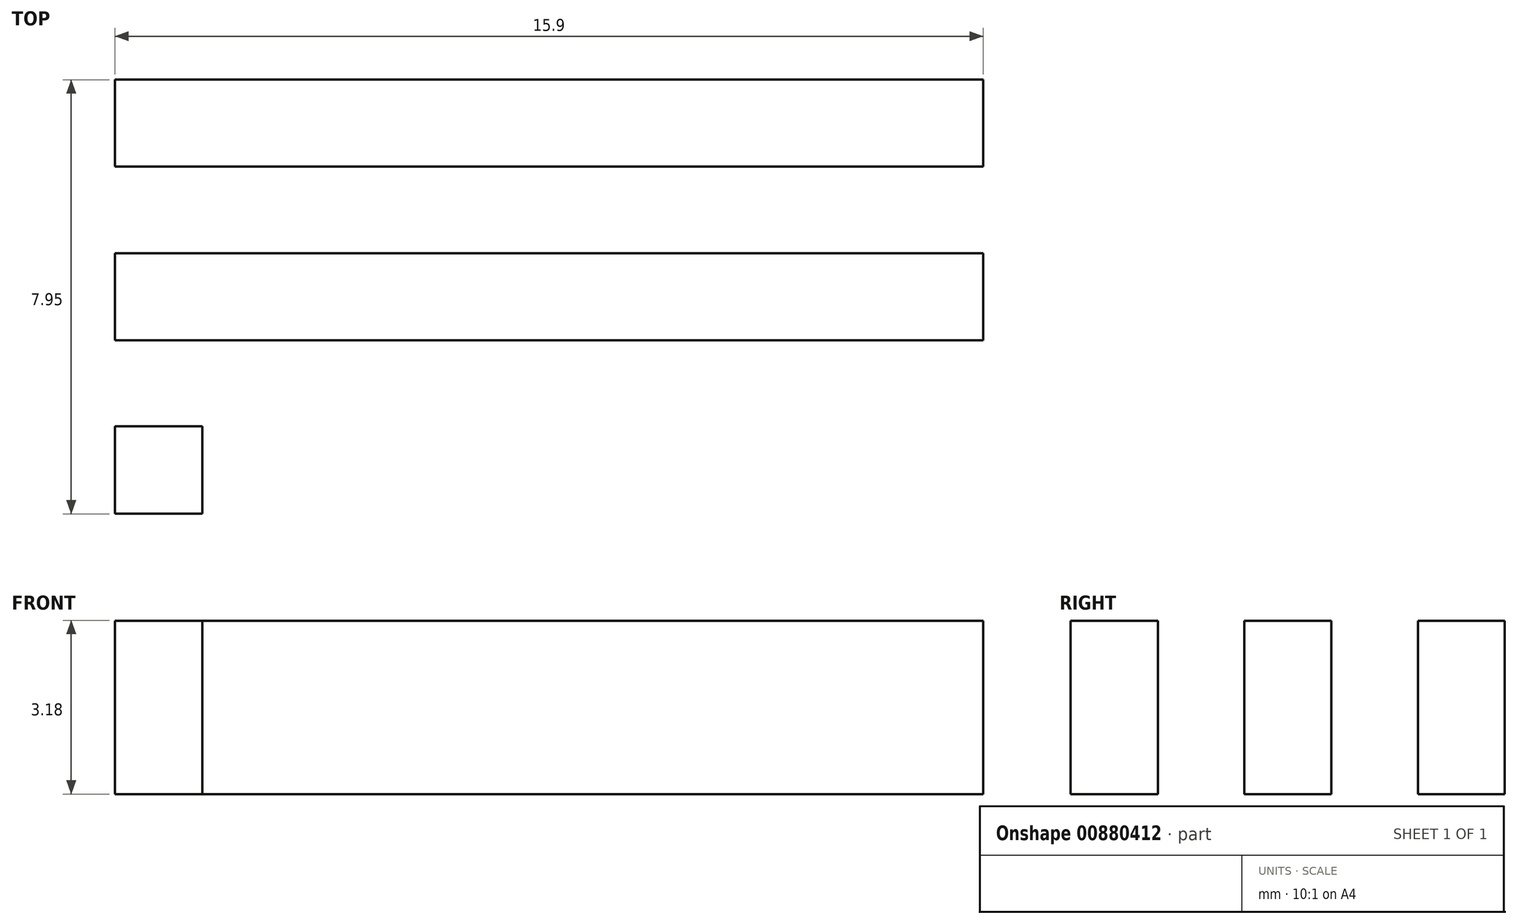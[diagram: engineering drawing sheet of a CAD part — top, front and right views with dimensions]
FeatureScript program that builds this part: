
annotation { "Feature Type Name" : "Feature", "Feature Type Description" : "" }
export const myFeature = defineFeature(function(context is Context, id is Id, definition is map)
    precondition{}
    {
        {
            var Q0;
            Q0=qCreatedBy(makeId("Top.planeOp"),FACE);
            var sketch = newSketch(context, id + "F0", { "sketchPlane" : qUnion([Q0])});
            skLineSegment(sketch, "E0.bottom", {"start": v(-6.6, -3.65) * mm, "end": v(9.3, -3.65) * mm});
            skLineSegment(sketch, "E0.top", {"start": v(-6.6, -11.6) * mm, "end": v(9.3, -11.6) * mm});
            skLineSegment(sketch, "E0.left", {"start": v(-6.6, -3.65) * mm, "end": v(-6.6, -11.6) * mm});
            skLineSegment(sketch, "E0.right", {"start": v(9.3, -3.65) * mm, "end": v(9.3, -11.6) * mm});
            skLineSegment(sketch, "E1", {"start": v(-6.6, -5.24) * mm, "end": v(9.3, -5.24) * mm});
            skLineSegment(sketch, "E2", {"start": v(-6.6, -6.83) * mm, "end": v(9.3, -6.83) * mm});
            skLineSegment(sketch, "E3", {"start": v(-6.6, -8.42) * mm, "end": v(9.3, -8.42) * mm});
            skLineSegment(sketch, "E4", {"start": v(9.3, -10) * mm, "end": v(-6.6, -10) * mm});
            skLineSegment(sketch, "E5", {"start": v(-5, -11.6) * mm, "end": v(-5, -3.65) * mm});
            skLineSegment(sketch, "E6", {"start": v(7.7, -11.6) * mm, "end": v(7.7, -3.65) * mm});
            skLineSegment(sketch, "E7", {"start": v(-6.6, -5.24) * mm, "end": v(-5, -5.24) * mm});
            skLineSegment(sketch, "E8", {"start": v(-5, -5.24) * mm, "end": v(-5, -6.83) * mm});
            skLineSegment(sketch, "E9", {"start": v(-5, -6.83) * mm, "end": v(-6.6, -6.83) * mm});
            skLineSegment(sketch, "E10", {"start": v(-6.6, -5.24) * mm, "end": v(-6.6, -6.83) * mm});
            skLineSegment(sketch, "E11", {"start": v(-6.6, -8.42) * mm, "end": v(-6.6, -10) * mm});
            skLineSegment(sketch, "E12", {"start": v(-5, -10) * mm, "end": v(-5, -8.42) * mm});
            skLineSegment(sketch, "E13", {"start": v(-5, -8.42) * mm, "end": v(-6.6, -8.42) * mm});
            skLineSegment(sketch, "E14", {"start": v(7.7, -5.24) * mm, "end": v(9.3, -5.24) * mm});
            skLineSegment(sketch, "E15", {"start": v(9.3, -6.83) * mm, "end": v(7.7, -6.83) * mm});
            skLineSegment(sketch, "E16", {"start": v(7.7, -6.83) * mm, "end": v(7.7, -5.24) * mm});
            skLineSegment(sketch, "E17", {"start": v(7.7, -10) * mm, "end": v(9.3, -10) * mm});
            skLineSegment(sketch, "E18", {"start": v(9.3, -11.6) * mm, "end": v(7.7, -11.6) * mm});
            skLineSegment(sketch, "E19", {"start": v(9.3, -10) * mm, "end": v(9.3, -11.6) * mm});
            skLineSegment(sketch, "E20", {"start": v(7.7, -11.6) * mm, "end": v(7.7, -10) * mm});
            skSolve(sketch);
        }
        {
            var Q0;
            {var subQ0=sQuery(id+"F0.wireOp",EDGE,"E17");Q0=makeQuery(id+"F0.imprint","IMPRINT",FACE,{"disambiguationData":[TD([[makeQuery(id+"F0.imprint","IMPRINT",EDGE,{"derivedFrom":subQ0}),1.0]])]});}
            var Q1;
            {var subQ5=sQuery(id+"F0.wireOp",EDGE,"E7");Q1=makeQuery(id+"F0.imprint","IMPRINT",FACE,{"disambiguationData":[TD([[makeQuery(id+"F0.imprint","IMPRINT",EDGE,{"derivedFrom":subQ5}),1.0]])]});}
            var Q2;
            {var subQ5=sQuery(id+"F0.wireOp",EDGE,"E14");Q2=makeQuery(id+"F0.imprint","IMPRINT",FACE,{"disambiguationData":[TD([[makeQuery(id+"F0.imprint","IMPRINT",EDGE,{"derivedFrom":subQ5}),1.0]])]});}
            var Q3;
            {var subQ5=sQuery(id+"F0.wireOp",EDGE,"E1");Q3=makeQuery(id+"F0.imprint","IMPRINT",FACE,{"disambiguationData":[TD([[makeQuery(id+"F0.imprint","IMPRINT",EDGE,{"derivedFrom":subQ5}),1.0]])]});}
            var Q4;
            {var subQ0=sQuery(id+"F0.wireOp",EDGE,"E2");Q4=makeQuery(id+"F0.imprint","IMPRINT",FACE,{"disambiguationData":[TD([[makeQuery(id+"F0.imprint","IMPRINT",EDGE,{"derivedFrom":subQ0}),-1.0]])]});}
            var Q5;
            {var subQ0=sQuery(id+"F0.wireOp",EDGE,"E0.left");var subQ1=sQuery(id+"F0.wireOp",EDGE,"E0.top");var subQ2=makeQuery(id+"F0.imprint","INTERSECT",VERTEX,{"derivedFrom":[subQ1,subQ0]});Q5=makeQuery(id+"F0.imprint","IMPRINT",FACE,{"disambiguationData":[TD([[makeQuery(id+"F0.imprint","IMPRINT",EDGE,{"disambiguationData":[TD([[subQ2,-1.0]])],"derivedFrom":subQ1}),1.0]])]});}
            var Q6;
            Q6=makeQuery(id+"F0.imprint","IMPRINT",FACE,{"disambiguationData":[TD([[makeQuery(id+"F0.imprint","IMPRINT",EDGE,{"derivedFrom":sQuery(id+"F0.wireOp",EDGE,"E7")}),-1.0]])]});
            var Q7;
            {var subQ0=sQuery(id+"F0.wireOp",EDGE,"E9");Q7=makeQuery(id+"F0.imprint","IMPRINT",FACE,{"disambiguationData":[TD([[makeQuery(id+"F0.imprint","IMPRINT",EDGE,{"derivedFrom":subQ0}),1.0]])]});}
            var Q8;
            {var subQ0=sQuery(id+"F0.wireOp",EDGE,"E11");Q8=makeQuery(id+"F0.imprint","IMPRINT",FACE,{"disambiguationData":[TD([[makeQuery(id+"F0.imprint","IMPRINT",EDGE,{"derivedFrom":subQ0}),1.0]])]});}
            var Q9;
            {var subQ0=sQuery(id+"F0.wireOp",EDGE,"E14");Q9=makeQuery(id+"F0.imprint","IMPRINT",FACE,{"disambiguationData":[TD([[makeQuery(id+"F0.imprint","IMPRINT",EDGE,{"derivedFrom":subQ0}),-1.0]])]});}
            var Q10;
            {var subQ3=sQuery(id+"F0.wireOp",EDGE,"E15");Q10=makeQuery(id+"F0.imprint","IMPRINT",FACE,{"disambiguationData":[TD([[makeQuery(id+"F0.imprint","IMPRINT",EDGE,{"derivedFrom":subQ3}),1.0]])]});}
            var Q11;
            Q11=makeQuery(id+"F0.imprint","IMPRINT",FACE,{"disambiguationData":[TD([[makeQuery(id+"F0.imprint","IMPRINT",EDGE,{"derivedFrom":sQuery(id+"F0.wireOp",EDGE,"E17")}),-1.0]])]});
            var Q12;
            Q12=makeQuery(id+"F0.imprint","IMPRINT",FACE,{"disambiguationData":[TD([[makeQuery(id+"F0.imprint","IMPRINT",EDGE,{"derivedFrom":sQuery(id+"F0.wireOp",EDGE,"E1")}),-1.0]])]});
            var Q13;
            {var subQ0=sQuery(id+"F0.wireOp",EDGE,"E12");Q13=makeQuery(id+"F0.imprint","IMPRINT",FACE,{"disambiguationData":[TD([[makeQuery(id+"F0.imprint","IMPRINT",EDGE,{"derivedFrom":subQ0}),-1.0]])]});}
            var Q14;
            {var subQ0=sQuery(id+"F0.wireOp",EDGE,"E20");Q14=makeQuery(id+"F0.imprint","IMPRINT",FACE,{"disambiguationData":[TD([[makeQuery(id+"F0.imprint","IMPRINT",EDGE,{"derivedFrom":subQ0}),1.0]])]});}
            extrude(context, id + "F1", {"entities" : qUnion([Q0, Q1, Q2, Q3, Q4, Q5, Q6, Q7, Q8, Q9, Q10, Q11, Q12, Q13, Q14]), "depth" : 3.17 * mm, "offsetDistance" : 25.4 * mm});
        }
        {
            var Q0;
            Q0=makeQuery(id+"F1.opExtrude","CAP_FACE",FACE,{"disambiguationData":[OSD([sQuery(id+"F0.wireOp",EDGE,"E0.bottom"),sQuery(id+"F0.wireOp",EDGE,"E0.top"),sQuery(id+"F0.wireOp",EDGE,"E0.left"),sQuery(id+"F0.wireOp",EDGE,"E0.right")])],"isStart":true});
            shell(context, id + "F2", {"entities" : qUnion([Q0]), "thickness" : 1.6 * mm});
        }
        {
            var Q0;
            Q0=makeQuery(id+"F0.imprint","IMPRINT",FACE,{"disambiguationData":[TD([[makeQuery(id+"F0.imprint","IMPRINT",EDGE,{"derivedFrom":sQuery(id+"F0.wireOp",EDGE,"E1")}),-1.0]])]});
            var Q1;
            {var subQ0=sQuery(id+"F0.wireOp",EDGE,"E12");Q1=makeQuery(id+"F0.imprint","IMPRINT",FACE,{"disambiguationData":[TD([[makeQuery(id+"F0.imprint","IMPRINT",EDGE,{"derivedFrom":subQ0}),-1.0]])]});}
            extrude(context, id + "F3", {"entities" : qUnion([Q0, Q1]), "operationType" : NewBodyOperationType.REMOVE, "depth" : 25.4 * mm, "offsetDistance" : 25.4 * mm});
        }
        {
            var Q0;
            Q0=makeQuery(id+"F1.opExtrude","CAP_FACE",FACE,{"disambiguationData":[OSD([sQuery(id+"F0.wireOp",EDGE,"E0.bottom"),sQuery(id+"F0.wireOp",EDGE,"E0.top"),sQuery(id+"F0.wireOp",EDGE,"E0.left"),sQuery(id+"F0.wireOp",EDGE,"E0.right"),sQuery(id+"F0.wireOp",EDGE,"E10"),sQuery(id+"F0.wireOp",EDGE,"E11"),sQuery(id+"F0.wireOp",EDGE,"E19"),sQuery(id+"F0.wireOp",EDGE,"E18")])],"isStart":false});
            var sketch = newSketch(context, id + "F4", { "sketchPlane" : qUnion([Q0])});
            skLineSegment(sketch, "E21.0", {"start": v(9.3, -10) * mm, "end": v(-6.6, -10) * mm});
            skLineSegment(sketch, "E22.0", {"start": v(-6.6, -8.42) * mm, "end": v(9.3, -8.42) * mm});
            skLineSegment(sketch, "E23.0", {"start": v(7.7, -11.6) * mm, "end": v(7.7, -3.65) * mm});
            skLineSegment(sketch, "E24.0", {"start": v(9.3, -3.65) * mm, "end": v(9.3, -11.6) * mm});
            skLineSegment(sketch, "E25.0", {"start": v(9.3, -6.83) * mm, "end": v(7.7, -6.83) * mm});
            skLineSegment(sketch, "E26.0", {"start": v(7.7, -5.24) * mm, "end": v(9.3, -5.24) * mm});
            skLineSegment(sketch, "E27.0", {"start": v(-5, -6.83) * mm, "end": v(-6.6, -6.83) * mm});
            skLineSegment(sketch, "E28.0", {"start": v(-5, -5.24) * mm, "end": v(-5, -6.83) * mm});
            skLineSegment(sketch, "E29.0", {"start": v(-6.6, -5.24) * mm, "end": v(-5, -5.24) * mm});
            skLineSegment(sketch, "E30.0", {"start": v(-6.6, -5.24) * mm, "end": v(-6.6, -6.83) * mm});
            skLineSegment(sketch, "E31.0", {"start": v(-6.6, -8.42) * mm, "end": v(-6.6, -10) * mm});
            skLineSegment(sketch, "E32.0", {"start": v(-5, -10) * mm, "end": v(-5, -8.42) * mm});
            skLineSegment(sketch, "E33.0.0", {"start": v(-5, -10) * mm, "end": v(7.7, -10) * mm});
            skLineSegment(sketch, "E33.0.1", {"start": v(7.7, -10) * mm, "end": v(7.7, -8.42) * mm});
            skLineSegment(sketch, "E33.0.2", {"start": v(7.7, -8.42) * mm, "end": v(-5, -8.42) * mm});
            skLineSegment(sketch, "E33.0.3", {"start": v(-5, -8.42) * mm, "end": v(-5, -10) * mm});
            skLineSegment(sketch, "E34.0.0", {"start": v(7.7, -5.24) * mm, "end": v(-5, -5.24) * mm});
            skLineSegment(sketch, "E34.0.2", {"start": v(-5, -6.83) * mm, "end": v(7.7, -6.83) * mm});
            skLineSegment(sketch, "E34.0.3", {"start": v(7.7, -6.83) * mm, "end": v(7.7, -5.24) * mm});
            skLineSegment(sketch, "E35", {"start": v(-6.6, -6.83) * mm, "end": v(-5, -6.83) * mm});
            skLineSegment(sketch, "E36", {"start": v(-5, -6.83) * mm, "end": v(-5, -5.24) * mm});
            skLineSegment(sketch, "E37", {"start": v(-5, -5.24) * mm, "end": v(-6.6, -5.24) * mm});
            skLineSegment(sketch, "E38", {"start": v(-6.6, -10) * mm, "end": v(-5, -10) * mm});
            skLineSegment(sketch, "E39", {"start": v(-5, -8.42) * mm, "end": v(-6.6, -8.42) * mm});
            skLineSegment(sketch, "E40", {"start": v(7.7, -8.42) * mm, "end": v(9.3, -8.42) * mm});
            skLineSegment(sketch, "E41", {"start": v(9.3, -8.42) * mm, "end": v(9.3, -10) * mm});
            skLineSegment(sketch, "E42", {"start": v(9.3, -10) * mm, "end": v(7.7, -10) * mm});
            skSolve(sketch);
        }
        {
            var Q0;
            Q0=makeQuery(id+"F4.imprint","IMPRINT",FACE,{"disambiguationData":[TD([[makeQuery(id+"F4.imprint","IMPRINT",EDGE,{"derivedFrom":sQuery(id+"F4.wireOp",EDGE,"E30.0")}),1.0]])]});
            var Q1;
            Q1=makeQuery(id+"F4.imprint","IMPRINT",FACE,{"disambiguationData":[TD([[makeQuery(id+"F4.imprint","IMPRINT",EDGE,{"derivedFrom":sQuery(id+"F4.wireOp",EDGE,"E31.0")}),1.0]])]});
            var Q2;
            {var subQ0=sQuery(id+"F4.wireOp",EDGE,"E25.0");Q2=makeQuery(id+"F4.imprint","IMPRINT",FACE,{"disambiguationData":[TD([[makeQuery(id+"F4.imprint","IMPRINT",EDGE,{"derivedFrom":subQ0}),-1.0]])]});}
            var Q3;
            Q3=makeQuery(id+"F4.imprint","IMPRINT",FACE,{"disambiguationData":[TD([[makeQuery(id+"F4.imprint","IMPRINT",EDGE,{"derivedFrom":sQuery(id+"F4.wireOp",EDGE,"E40")}),-1.0]])]});
            extrude(context, id + "F5", {"entities" : qUnion([Q0, Q1, Q2, Q3]), "operationType" : NewBodyOperationType.REMOVE, "oppositeDirection" : true, "depth" : 1.6 * mm, "offsetDistance" : 25.4 * mm});
        }
    });
